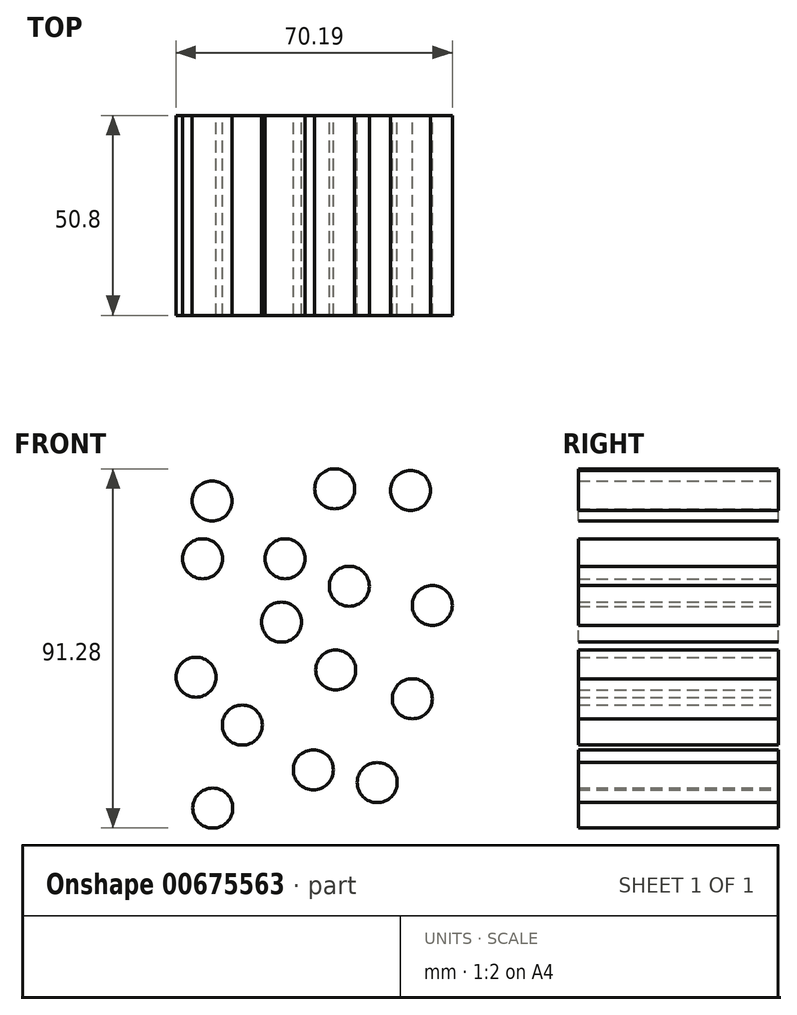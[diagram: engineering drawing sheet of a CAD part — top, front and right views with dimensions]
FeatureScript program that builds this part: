
annotation { "Feature Type Name" : "Feature", "Feature Type Description" : "" }
export const myFeature = defineFeature(function(context is Context, id is Id, definition is map)
    precondition{}
    {
        {
            var Q0;
            Q0=qCreatedBy(makeId("Front.planeOp"),FACE);
            var sketch = newSketch(context, id + "F0", { "sketchPlane" : qUnion([Q0])});
            skCircle(sketch, "E0", {"center": v(-62.92, 47.64) * mm, "radius": 5.08 * mm});
            skSolve(sketch);
        }
        {
            var Q0;
            Q0 = qSketchRegion(id + "F0", true);
            extrude(context, id + "F1", {"entities" : qUnion([Q0]), "depth" : 50.8 * mm, "offsetDistance" : 25.4 * mm});
        }
        {
            var Q0;
            Q0=qCreatedBy(makeId("Front.planeOp"),FACE);
            var sketch = newSketch(context, id + "F2", { "sketchPlane" : qUnion([Q0])});
            skCircle(sketch, "E1", {"center": v(-31.8, 50.7) * mm, "radius": 5.08 * mm});
            skSolve(sketch);
        }
        {
            var Q0;
            Q0 = qSketchRegion(id + "F2", true);
            extrude(context, id + "F3", {"entities" : qUnion([Q0]), "depth" : 50.8 * mm, "offsetDistance" : 25.4 * mm});
        }
        {
            var Q0;
            Q0=qCreatedBy(makeId("Front.planeOp"),FACE);
            var sketch = newSketch(context, id + "F4", { "sketchPlane" : qUnion([Q0])});
            skCircle(sketch, "E2", {"center": v(-12.5, 50.32) * mm, "radius": 5.08 * mm});
            skSolve(sketch);
        }
        {
            var Q0;
            Q0 = qSketchRegion(id + "F4", true);
            extrude(context, id + "F5", {"entities" : qUnion([Q0]), "depth" : 50.8 * mm, "offsetDistance" : 25.4 * mm});
        }
        {
            var Q0;
            Q0=qCreatedBy(makeId("Front.planeOp"),FACE);
            var sketch = newSketch(context, id + "F6", { "sketchPlane" : qUnion([Q0])});
            skCircle(sketch, "E3", {"center": v(-65.34, 32.94) * mm, "radius": 5.08 * mm});
            skSolve(sketch);
        }
        {
            var Q0;
            Q0 = qSketchRegion(id + "F6", true);
            extrude(context, id + "F7", {"entities" : qUnion([Q0]), "depth" : 50.8 * mm, "offsetDistance" : 25.4 * mm});
        }
        {
            var Q0;
            Q0=qCreatedBy(makeId("Front.planeOp"),FACE);
            var sketch = newSketch(context, id + "F8", { "sketchPlane" : qUnion([Q0])});
            skCircle(sketch, "E4", {"center": v(-44.4, 32.94) * mm, "radius": 5.08 * mm});
            skSolve(sketch);
        }
        {
            var Q0;
            Q0 = qSketchRegion(id + "F8", true);
            extrude(context, id + "F9", {"entities" : qUnion([Q0]), "depth" : 50.8 * mm, "offsetDistance" : 25.4 * mm});
        }
        {
            var Q0;
            Q0=qCreatedBy(makeId("Front.planeOp"),FACE);
            var sketch = newSketch(context, id + "F10", { "sketchPlane" : qUnion([Q0])});
            skCircle(sketch, "E5", {"center": v(-45.33, 16.83) * mm, "radius": 5.08 * mm});
            skCircle(sketch, "E6", {"center": v(-28.09, 25.96) * mm, "radius": 5.08 * mm});
            skCircle(sketch, "E7", {"center": v(-31.54, 4.66) * mm, "radius": 5.08 * mm});
            skCircle(sketch, "E8", {"center": v(-67.03, 2.84) * mm, "radius": 5.08 * mm});
            skCircle(sketch, "E9", {"center": v(-7, 21.1) * mm, "radius": 5.08 * mm});
            skCircle(sketch, "E10", {"center": v(-12.07, -2.64) * mm, "radius": 5.08 * mm});
            skCircle(sketch, "E11", {"center": v(-55.27, -9.33) * mm, "radius": 5.08 * mm});
            skCircle(sketch, "E12", {"center": v(-37.22, -20.69) * mm, "radius": 5.08 * mm});
            skCircle(sketch, "E13", {"center": v(-21, -23.93) * mm, "radius": 5.08 * mm});
            skCircle(sketch, "E14", {"center": v(-62.77, -30.42) * mm, "radius": 5.08 * mm});
            skSolve(sketch);
        }
        {
            var Q0;
            Q0 = qSketchRegion(id + "F10", true);
            extrude(context, id + "F11", {"entities" : qUnion([Q0]), "depth" : 50.8 * mm, "offsetDistance" : 25.4 * mm});
        }
    });
